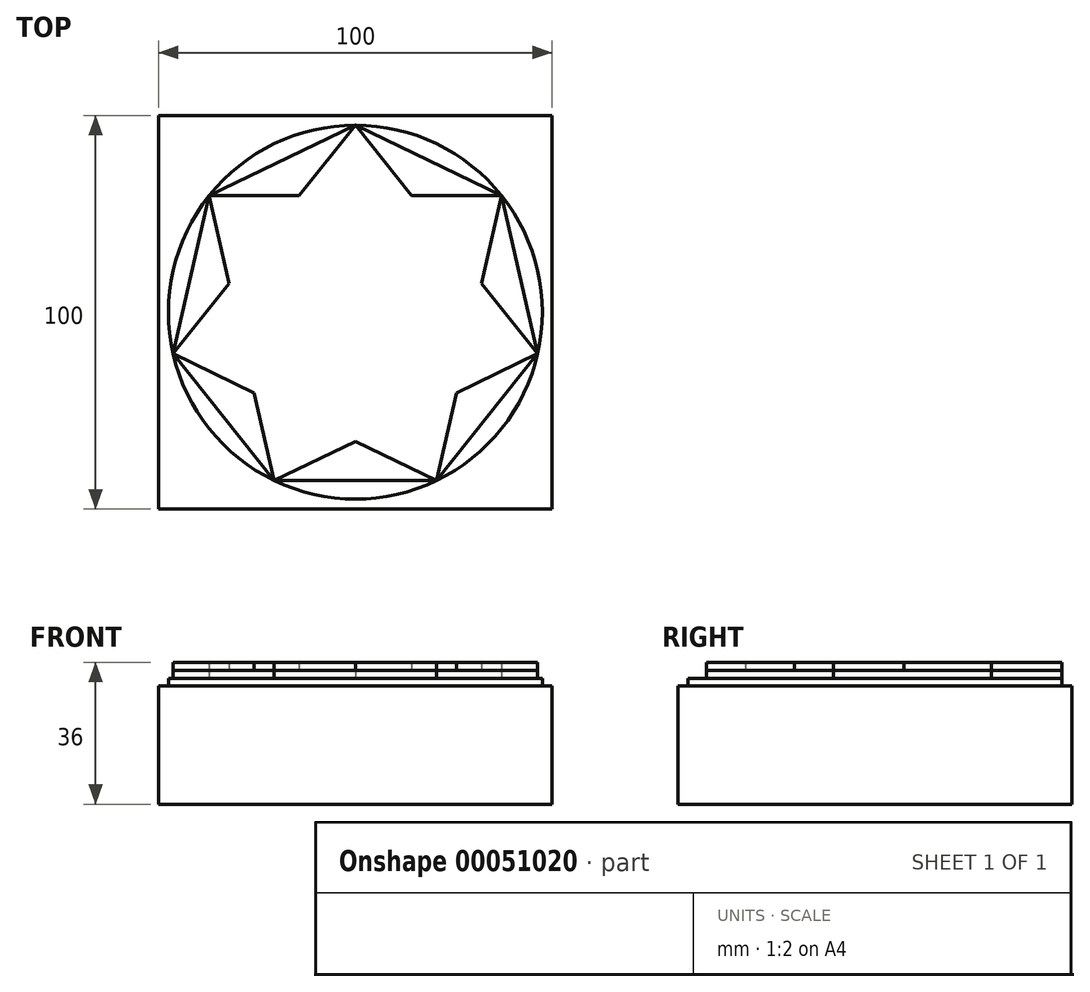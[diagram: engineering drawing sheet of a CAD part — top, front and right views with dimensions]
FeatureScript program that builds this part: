
annotation { "Feature Type Name" : "Feature", "Feature Type Description" : "" }
export const myFeature = defineFeature(function(context is Context, id is Id, definition is map)
    precondition{}
    {
        {
            var Q0;
            Q0=qCreatedBy(makeId("Top.planeOp"),FACE);
            var sketch = newSketch(context, id + "F0", { "sketchPlane" : qUnion([Q0])});
            skLineSegment(sketch, "E0.rect.bottom", {"start": v(-50, 50) * mm, "end": v(50, 50) * mm});
            skLineSegment(sketch, "E0.rect.top", {"start": v(-50, -50) * mm, "end": v(50, -50) * mm});
            skLineSegment(sketch, "E0.rect.left", {"start": v(-50, 50) * mm, "end": v(-50, -50) * mm});
            skLineSegment(sketch, "E0.rect.right", {"start": v(50, 50) * mm, "end": v(50, -50) * mm});
            skPoint(sketch, "E0.rect.middle", {"position": v(0, 0) * mm});
            skSolve(sketch);
        }
        {
            var Q0;
            Q0 = qSketchRegion(id + "F0", true);
            var Q1;
            Q1=makeQuery(id+"F0.imprint","IMPRINT",FACE,{"disambiguationData":[TD([[makeQuery(id+"F0.imprint","IMPRINT",EDGE,{"derivedFrom":sQuery(id+"F0.wireOp",EDGE,"E0.rect.bottom")}),-1.0]])]});
            extrude(context, id + "F1", {"entities" : qUnion([Q0, Q1]), "depth" : 30 * mm});
        }
        {
            var Q0;
            Q0=makeQuery(id+"F1.opExtrude","CAP_FACE",FACE,{"disambiguationData":[OSD([sQuery(id+"F0.wireOp",EDGE,"E0.rect.bottom"),sQuery(id+"F0.wireOp",EDGE,"E0.rect.top"),sQuery(id+"F0.wireOp",EDGE,"E0.rect.left"),sQuery(id+"F0.wireOp",EDGE,"E0.rect.right")])],"isStart":false});
            var sketch = newSketch(context, id + "F2", { "sketchPlane" : qUnion([Q0])});
            skCircle(sketch, "E1", {"center": v(0, 0) * mm, "radius": 47.5 * mm});
            skSolve(sketch);
        }
        {
            var Q0;
            Q0 = qSketchRegion(id + "F2", true);
            extrude(context, id + "F3", {"entities" : qUnion([Q0]), "operationType" : NewBodyOperationType.ADD, "depth" : 2 * mm});
        }
        {
            var Q0;
            Q0=makeQuery(id+"F3.opExtrude","CAP_FACE",FACE,{"disambiguationData":[OSD([sQuery(id+"F2.wireOp",EDGE,"E1")])],"isStart":false});
            var sketch = newSketch(context, id + "F4", { "sketchPlane" : qUnion([Q0])});
            skCircle(sketch, "E2.cCircle", {"center": v(0, 0) * mm, "radius": 47.5 * mm, "construction": true});
            skLineSegment(sketch, "E2.0", {"start": v(0, 47.5) * mm, "end": v(37.14, 29.62) * mm});
            skLineSegment(sketch, "E2.1", {"start": v(37.14, 29.62) * mm, "end": v(46.3, -10.57) * mm});
            skLineSegment(sketch, "E2.2", {"start": v(46.3, -10.57) * mm, "end": v(20.6, -42.8) * mm});
            skLineSegment(sketch, "E2.3", {"start": v(20.6, -42.8) * mm, "end": v(-20.6, -42.8) * mm});
            skLineSegment(sketch, "E2.4", {"start": v(-20.6, -42.8) * mm, "end": v(-46.3, -10.57) * mm});
            skLineSegment(sketch, "E2.5", {"start": v(-46.3, -10.57) * mm, "end": v(-37.14, 29.62) * mm});
            skLineSegment(sketch, "E2.6", {"start": v(-37.14, 29.62) * mm, "end": v(0, 47.5) * mm});
            skSolve(sketch);
        }
        {
            var Q0;
            Q0=makeQuery(id+"F4.imprint","IMPRINT",FACE,{"disambiguationData":[TD([[makeQuery(id+"F4.imprint","IMPRINT",EDGE,{"derivedFrom":sQuery(id+"F4.wireOp",EDGE,"E2.0")}),-1.0]])]});
            extrude(context, id + "F5", {"entities" : qUnion([Q0]), "operationType" : NewBodyOperationType.ADD, "depth" : 2 * mm});
        }
        {
            var Q0;
            Q0=makeQuery(id+"F5.opExtrude","CAP_FACE",FACE,{"disambiguationData":[OSD([sQuery(id+"F4.wireOp",EDGE,"E2.0"),sQuery(id+"F4.wireOp",EDGE,"E2.1"),sQuery(id+"F4.wireOp",EDGE,"E2.2"),sQuery(id+"F4.wireOp",EDGE,"E2.3"),sQuery(id+"F4.wireOp",EDGE,"E2.4"),sQuery(id+"F4.wireOp",EDGE,"E2.5"),sQuery(id+"F4.wireOp",EDGE,"E2.6")])],"isStart":false});
            var sketch = newSketch(context, id + "F6", { "sketchPlane" : qUnion([Q0])});
            skLineSegment(sketch, "E3", {"start": v(-20.6, -42.8) * mm, "end": v(-25.7, -20.5) * mm});
            skLineSegment(sketch, "E4", {"start": v(-37.14, 29.62) * mm, "end": v(-14.26, 29.62) * mm});
            skLineSegment(sketch, "E5", {"start": v(37.14, 29.62) * mm, "end": v(32.05, 7.31) * mm});
            skLineSegment(sketch, "E6", {"start": v(20.6, -42.8) * mm, "end": v(0, -32.87) * mm});
            skLineSegment(sketch, "E7", {"start": v(-46.3, -10.57) * mm, "end": v(-32.05, 7.31) * mm});
            skLineSegment(sketch, "E8", {"start": v(0, 47.5) * mm, "end": v(14.26, 29.62) * mm});
            skLineSegment(sketch, "E9", {"start": v(46.3, -10.57) * mm, "end": v(25.7, -20.5) * mm});
            skLineSegment(sketch, "E10.trimOffspring", {"start": v(-14.26, 29.62) * mm, "end": v(0, 47.5) * mm});
            skLineSegment(sketch, "E11.trimOffspring", {"start": v(32.05, 7.31) * mm, "end": v(46.3, -10.57) * mm});
            skLineSegment(sketch, "E12.trimOffspring", {"start": v(25.7, -20.5) * mm, "end": v(20.6, -42.8) * mm});
            skLineSegment(sketch, "E13.trimOffspring", {"start": v(0, -32.87) * mm, "end": v(-20.6, -42.8) * mm});
            skLineSegment(sketch, "E14.trimOffspring", {"start": v(-25.7, -20.5) * mm, "end": v(-46.3, -10.57) * mm});
            skLineSegment(sketch, "E15.trimOffspring", {"start": v(-32.05, 7.31) * mm, "end": v(-37.14, 29.62) * mm});
            skLineSegment(sketch, "E16.trimOffspring", {"start": v(14.26, 29.62) * mm, "end": v(37.14, 29.62) * mm});
            skSolve(sketch);
        }
        {
            var Q0;
            Q0 = qSketchRegion(id + "F6", true);
            var Q1;
            {var subQ5=sQuery(id+"F6.wireOp",EDGE,"E6");var subQ6=sQuery(id+"F6.wireOp",EDGE,"E3");var subQ7=makeQuery(id+"F6.imprint","INTERSECT",VERTEX,{"derivedFrom":[subQ6,subQ5]});Q1=makeQuery(id+"F6.imprint","IMPRINT",FACE,{"disambiguationData":[TD([[makeQuery(id+"F6.imprint","IMPRINT",EDGE,{"disambiguationData":[TD([[subQ7,-1.0]])],"derivedFrom":subQ6}),-1.0]])]});}
            extrude(context, id + "F7", {"entities" : qUnion([Q0, Q1]), "operationType" : NewBodyOperationType.ADD, "depth" : 2 * mm});
        }
    });
